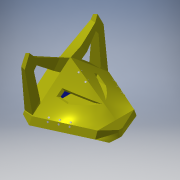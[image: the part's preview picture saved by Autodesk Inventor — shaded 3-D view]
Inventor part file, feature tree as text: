
AUTODESK INVENTOR PART (.ipt)
format: ipt  version: 2017.2 (Build 212233000, 233)  size: 763,904 bytes
history: native  units: in
note: dims shown in document units (in); Inventor stores cm internally (conversion verified against a paired STEP export)
features: sketch x22, extrude x16, plane x9, projected_geometry x5, loft x4, other x3, chamfer x1, mirror x1, emboss x1, fillet x1
ambient origin geometry x8: Origin, YZ Plane, XZ Plane, XY Plane, X Axis, Y Axis, Z Axis, Center Point
bodies: Solid1 (feature_tree)
feature tree (63):
  sketch  "Sketch1"  dims[d0=0.7559in d1=0.7559in]
  plane  "Work Plane1"
  loft  "Loft1"
  extrude  "Extrusion1"  Depth=0.2in
  plane  "Work Plane4"
  loft  "Loft2"
  plane  "Work Plane5"
  loft  "Loft3"
  loft  "Loft4"
  extrude  "Extrusion2"  TaperAngle=0.0deg  [1 undecoded]
  plane  "Work Plane6"
  extrude  "Extrusion3"  Depth=1.0in
  extrude  "Extrusion4"  Depth=1.0651in
  extrude  "Extrusion5"  Depth=0.962in
  plane  "Work Plane7"
  extrude  "Extrusion6"  Depth=0.075in
  plane  "Work Plane8"
  other  "Work Axis1"
  plane  "Work Plane9"
  chamfer  "Chamfer1"  Distance=0.45in
  extrude  "Extrusion7"  Depth=0.01in
  mirror  "Mirror3"
  extrude  "Extrusion8"  Depth=0.01in
  plane  "Work Plane10"
  extrude  "Extrusion9"  TaperAngle=0.0deg  [1 undecoded]
  plane  "Work Plane11"
  extrude  "Extrusion10"  Depth=0.07in
  extrude  "Extrusion11"  TaperAngle=0.0deg  [1 undecoded]
  extrude  "Extrusion12"  Depth=0.01in
  extrude  "Extrusion13"  TaperAngle=150.0deg  [1 undecoded]
  emboss  "Emboss1"
  extrude  "Extrusion16"  TaperAngle=150.0deg  [1 undecoded]
  extrude  "Extrusion17"  Depth=0.7in
  extrude  "Extrusion18"  Depth=0.05in
  fillet  "Fillet2"  Radius=0.05in
  sketch  "Sketch2"  dims[d2=0.9963in d3=0.2in]
  sketch  "Sketch3"  dims[d4=0.5in d6=0.08in]
  sketch  "Sketch4"  dims[d7=0.55in d8=150.0deg]
  other  "Edges1"
  sketch  "Sketch5"  dims[d9=150.0deg d14=0.33in]
  projected_geometry  "Projected Loop1"
  other  "Edges2"
  sketch  "Sketch6"  dims[d15=0.66in d18=0.0in d19=90.0deg]
  sketch  "Sketch7"  dims[d20=0.0in d21=90.0deg d22=1.0in]
  sketch  "Sketch8"  dims[d26=1.0651in d28=1.0651in]
  sketch  "Sketch9"  dims[d29=0.0in d30=0.962in]
  sketch  "Sketch10"  dims[d31=0.962in d32=0.075in]
  sketch  "Sketch11"  dims[d33=0.15in]
  sketch  "Sketch12"  dims[d34=0.06in]
  sketch  "Sketch13"  dims[d35=0.1in]
  projected_geometry  "Projected Loop2"
  projected_geometry  "Projected Loop3"
  sketch  "Sketch14"  dims[d36=0.05in d37=0.45in d38=0.0in]
  projected_geometry  "Projected Loop4"
  sketch  "Sketch15"  dims[d39=0.0625in d40=0.01in]
  sketch  "Sketch16"  dims[d41=0.075in d42=0.01in]
  sketch  "Sketch17"  dims[d43=0.0in d44=90.0deg d45=0.0in d46=90.0deg]
  sketch  "Sketch18"  dims[d47=0.2in d48=0.07in]
  sketch  "Sketch19"  dims[d49=0.0in d50=90.0deg d51=0.0in d52=90.0deg]
  sketch  "Sketch23"  dims[d53=0.01in d54=0.01in]
  projected_geometry  "Projected Loop6"
  sketch  "Sketch24"  dims[d55=0.0344in d56=150.0deg]
  sketch  "Sketch25"  dims[d57=60.0deg d58=150.0deg d59=0.7in d60=0.05in d61=0.05in d62=0.05in d63=0.05in d64=0.05in d65=0.01in d66=0.0in d67=90.0deg d68=0.0in d69=90.0deg d70=0.1in d71=0.4in d72=0.15in d73=0.05in d74=0.0in d75=0.02in d77=0.15in d78=0.02in d79=0.1in d80=0.1in d81=0.1in d82=0.02in d83=0.15in d84=0.05in d85=0.0in d86=0.045in d87=0.0in d88=0.025in d89=0.0in d90=0.02in d91=0.02in d92=0.005in d93=0.0in d94=90.0deg d95=0.4466in d96=1.0in d97=0.0in d98=1.0in d99=0.0in d100=0.6528in d101=0.0in d102=0.0in d103=1.0in d104=0.0in d106=90.0deg d107=1.0in d108=0.0in d109=1.65in d110=0.1in d111=0.1in d112=0.0in d113=0.1in d114=0.075in d115=0.0in d116=0.05in d117=0.0in d123=0.84in d124=0.8in d125=0.0in d126=0.0in d127=1.0in d128=0.0in d130=0.225in d131=-0.0206in d133=0.2125in d134=0.1125in d135=0.07in d136=0.1in d137=0.02in d138=0.125in d139=45.0deg]
note: 5 required parameter values undecoded (feature->parameter linkage not recoverable at this tier; creation-order binding heuristic only, values carry confidence <= 0.55)
